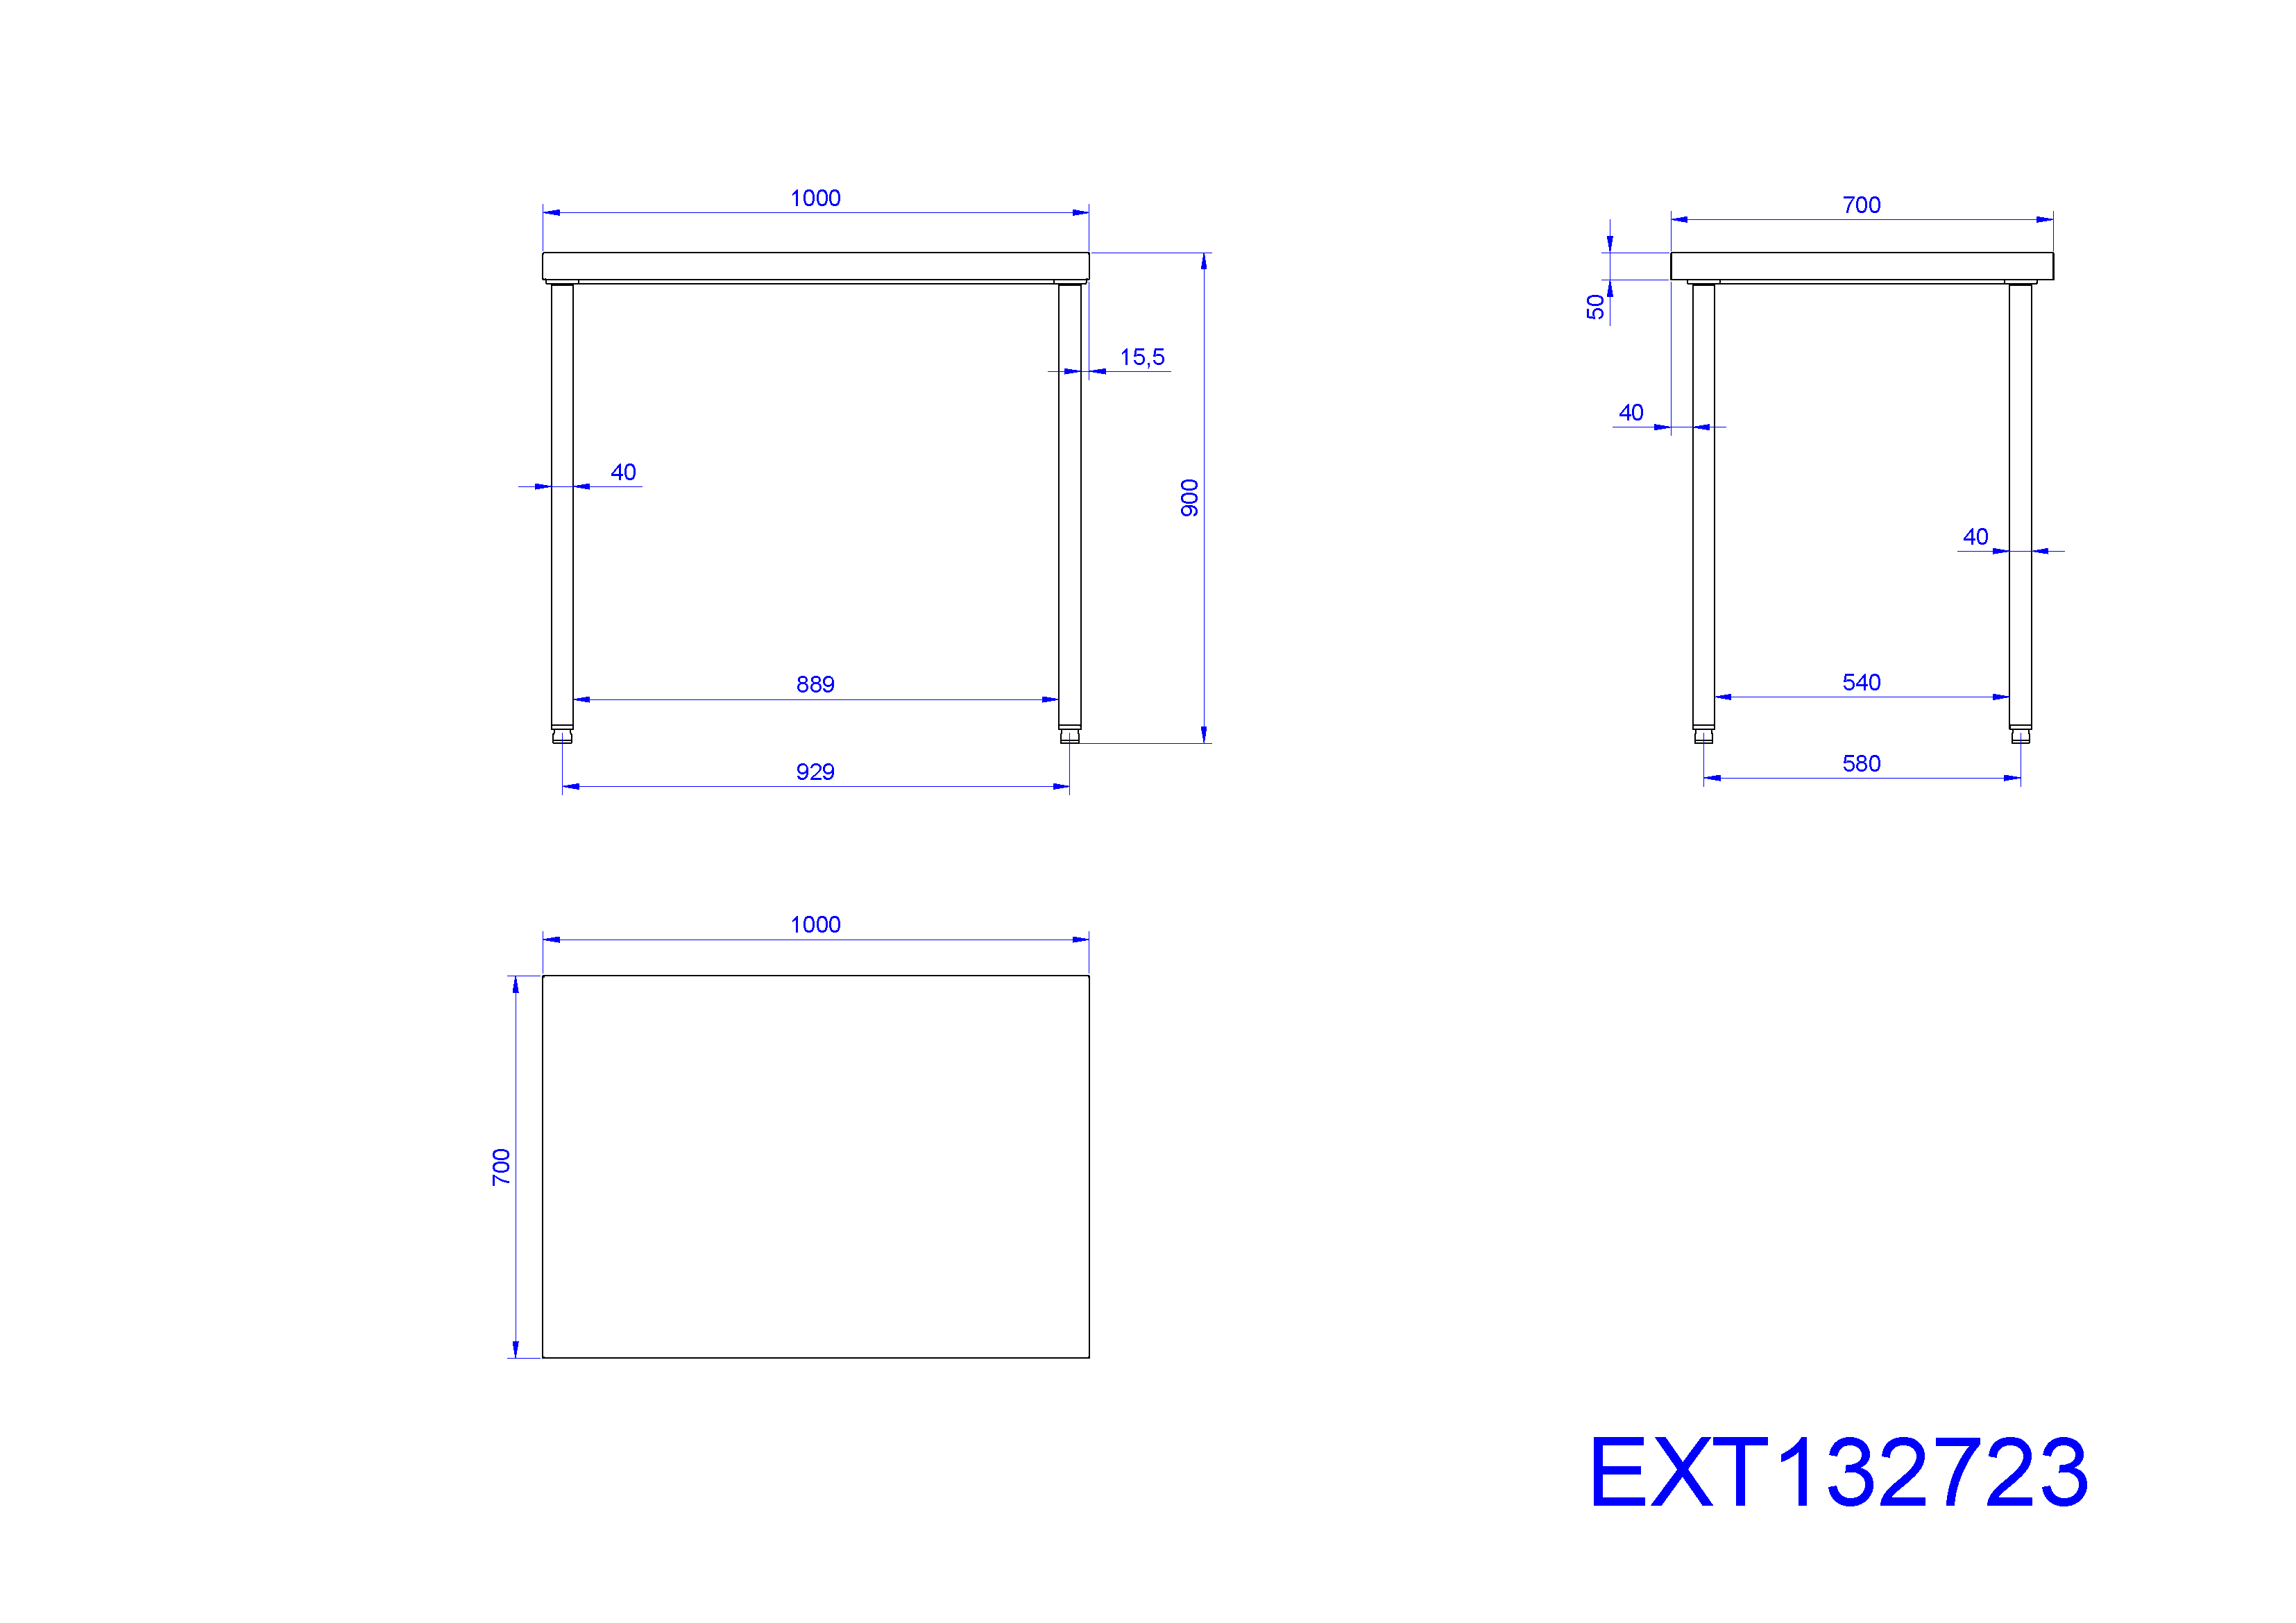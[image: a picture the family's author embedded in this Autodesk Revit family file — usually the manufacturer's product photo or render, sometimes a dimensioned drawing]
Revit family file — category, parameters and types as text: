
# Revit family: QF_ELECTROLUXPROFESSIONAL_133250_MLA1416SXPN
name_source: partatom
category: Attrezzature speciali
units: mm (PartAtom-declared; Revit-internal decimal feet)

## family parameters
Basato su piano di lavoro = No
Condiviso = No
Punto di calcolo locali = No
Quota connettore circolare = Usa diametro
Sempre verticale = Sì
Taglio con vuoti quando caricato = No
Tipo di parte = Normale

## types (1)
- Standard
    Accessory = Sì
    Cold Water Size = 0 mm
    Compressed Air Pressure = 0.0 Pa
    Compressed Air Size = 0 mm
    Compressed Air Volume = 0.0 L/s
    Condensate Return Size = 0 mm
    Cycle = 0 Hz
    Depth Actual = 700 mm  [stored 2.29659 ft]
    Descrizione = CUPBOARD SINK 1 BOWL+L/H DRAINER 1400MM
    Direct Waste Size = 51 mm
    Gas Input Pressure = 0
    Gas KW = 0
    Gas Size = 0 mm
    HP = 0 HP
    Height Actual = 1000 mm  [stored 3.28084 ft]
    Hot Water Size = 0 mm
    Item Number = 133250
    Length Actual = 1400 mm  [stored 4.59318 ft]
    Modello = MLA1416SXPN
    Phase = 0
    Produttore = Electrolux Professional
    Prospetto di default = 0 mm  [stored 0 ft]
    Refrigerant Compressor Remote = Sì
    Refrigeration Liquid Line Size = 0 mm  [stored 0 ft]
    Refrigeration Suction Line Size = 0 mm  [stored 0 ft]
    Steam Consumption per Hour = 0
    Steam Supply Maximum Pressure = 0.0 Pa
    Steam Supply Minimum Pressure = 0.0 Pa
    Steam Supply Size = 0 mm
    URL = https://www.electroluxprofessional.com
    URL Manufacturer = https://www.electroluxprofessional.com
    Volts = 0 V
    Watts = 0 W
    Weight = 60.00 kg

note: source unit labels omitted for Gas Input Pressure — the stored unit's dimension contradicts the parameter name (converter mislabeling)

note: [stored X ft] marks values corroborated as IEEE doubles in the binary element streams (Revit-internal decimal feet)

## geometry (parser evidence)
native form markers: Blend x4, Sweep x3
no freeform markers — native parametric forms only
